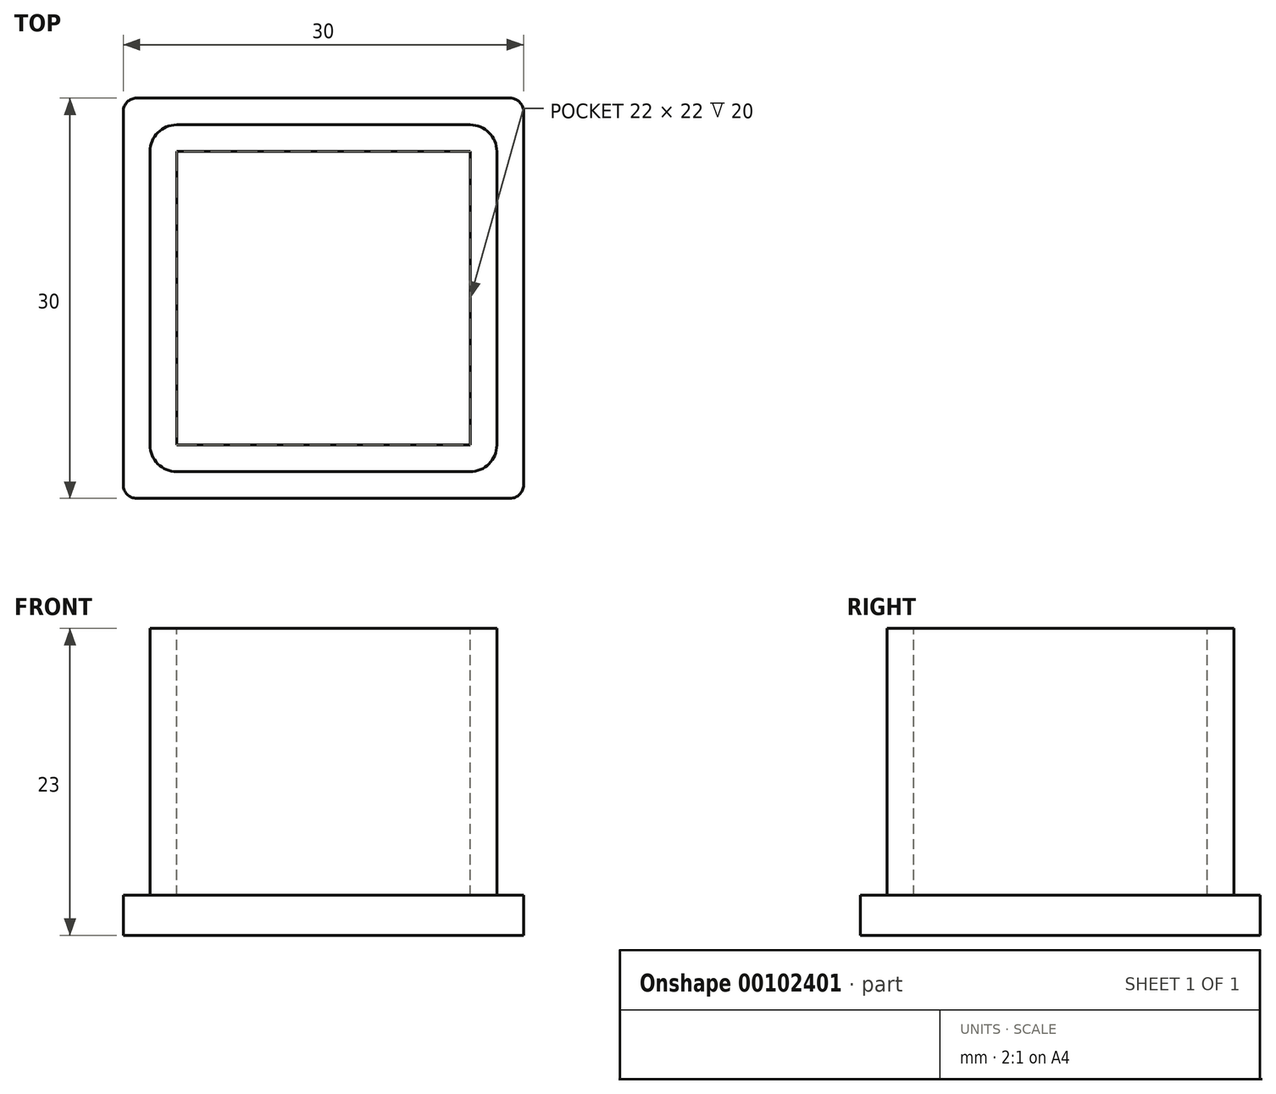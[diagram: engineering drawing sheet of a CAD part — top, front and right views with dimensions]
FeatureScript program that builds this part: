
annotation { "Feature Type Name" : "Feature", "Feature Type Description" : "" }
export const myFeature = defineFeature(function(context is Context, id is Id, definition is map)
    precondition{}
    {
        {
            var Q0;
            Q0=qCreatedBy(makeId("Top.planeOp"),FACE);
            var sketch = newSketch(context, id + "F0", { "sketchPlane" : qUnion([Q0])});
            skLineSegment(sketch, "E0.bottom", {"start": v(15, 15) * mm, "end": v(-15, 15) * mm});
            skLineSegment(sketch, "E0.top", {"start": v(15, -15) * mm, "end": v(-15, -15) * mm});
            skLineSegment(sketch, "E0.left", {"start": v(15, 15) * mm, "end": v(15, -15) * mm});
            skLineSegment(sketch, "E0.right", {"start": v(-15, 15) * mm, "end": v(-15, -15) * mm});
            skPoint(sketch, "E0.middle", {"position": v(0, 0) * mm});
            skSolve(sketch);
        }
        {
            var Q0;
            Q0=makeQuery(id+"F0.imprint","IMPRINT",FACE,{"disambiguationData":[TD([[makeQuery(id+"F0.imprint","IMPRINT",EDGE,{"derivedFrom":sQuery(id+"F0.wireOp",EDGE,"E0.bottom")}),1.0]])]});
            extrude(context, id + "F1", {"entities" : qUnion([Q0]), "depth" : 3 * mm});
        }
        {
            var Q0;
            Q0=makeQuery(id+"F1.opExtrude","SWEPT_EDGE",EDGE,{"disambiguationData":[OSD([sQuery(id+"F0.wireOp",EDGE,"E0.bottom"),sQuery(id+"F0.wireOp",EDGE,"E0.right")])]});
            var Q1;
            Q1=makeQuery(id+"F1.opExtrude","SWEPT_EDGE",EDGE,{"disambiguationData":[OSD([sQuery(id+"F0.wireOp",EDGE,"E0.top"),sQuery(id+"F0.wireOp",EDGE,"E0.right")])]});
            var Q2;
            Q2=makeQuery(id+"F1.opExtrude","SWEPT_EDGE",EDGE,{"disambiguationData":[OSD([sQuery(id+"F0.wireOp",EDGE,"E0.top"),sQuery(id+"F0.wireOp",EDGE,"E0.left")])]});
            var Q3;
            Q3=makeQuery(id+"F1.opExtrude","SWEPT_EDGE",EDGE,{"disambiguationData":[OSD([sQuery(id+"F0.wireOp",EDGE,"E0.bottom"),sQuery(id+"F0.wireOp",EDGE,"E0.left")])]});
            fillet(context, id + "F2", {"entities" : qUnion([Q0, Q1, Q2, Q3]), "radius" : 1 * mm, "tangentPropagation" : true, "allowEdgeOverflow" : false});
        }
        {
            var Q0;
            Q0=makeQuery(id+"F1.opExtrude","CAP_FACE",FACE,{"disambiguationData":[OSD([sQuery(id+"F0.wireOp",EDGE,"E0.bottom"),sQuery(id+"F0.wireOp",EDGE,"E0.top"),sQuery(id+"F0.wireOp",EDGE,"E0.left"),sQuery(id+"F0.wireOp",EDGE,"E0.right")])],"isStart":false});
            var sketch = newSketch(context, id + "F3", { "sketchPlane" : qUnion([Q0])});
            skLineSegment(sketch, "E1.0", {"start": v(13, -13) * mm, "end": v(13, 13) * mm});
            skLineSegment(sketch, "E1.1", {"start": v(-13, -13) * mm, "end": v(13, -13) * mm});
            skLineSegment(sketch, "E1.2", {"start": v(-13, 13) * mm, "end": v(-13, -13) * mm});
            skLineSegment(sketch, "E1.3", {"start": v(13, 13) * mm, "end": v(-13, 13) * mm});
            skSolve(sketch);
        }
        {
            var Q0;
            Q0 = qSketchRegion(id + "F3", true);
            var Q1;
            Q1=makeQuery(id+"F3.imprint","IMPRINT",FACE,{"disambiguationData":[TD([[makeQuery(id+"F3.imprint","IMPRINT",EDGE,{"derivedFrom":sQuery(id+"F3.wireOp",EDGE,"E1.0")}),1.0]])]});
            extrude(context, id + "F4", {"entities" : qUnion([Q0, Q1]), "operationType" : NewBodyOperationType.ADD, "depth" : 20 * mm});
        }
        {
            var Q0;
            Q0=makeQuery(id+"F4.opExtrude","SWEPT_EDGE",EDGE,{"disambiguationData":[OSD([sQuery(id+"F3.wireOp",EDGE,"E1.1"),sQuery(id+"F3.wireOp",EDGE,"E1.2")])]});
            var Q1;
            Q1=makeQuery(id+"F4.opExtrude","SWEPT_EDGE",EDGE,{"disambiguationData":[OSD([sQuery(id+"F3.wireOp",EDGE,"E1.0"),sQuery(id+"F3.wireOp",EDGE,"E1.1")])]});
            var Q2;
            Q2=makeQuery(id+"F4.opExtrude","SWEPT_EDGE",EDGE,{"disambiguationData":[OSD([sQuery(id+"F3.wireOp",EDGE,"E1.0"),sQuery(id+"F3.wireOp",EDGE,"E1.3")])]});
            var Q3;
            Q3=makeQuery(id+"F4.opExtrude","SWEPT_EDGE",EDGE,{"disambiguationData":[OSD([sQuery(id+"F3.wireOp",EDGE,"E1.2"),sQuery(id+"F3.wireOp",EDGE,"E1.3")])]});
            fillet(context, id + "F5", {"entities" : qUnion([Q0, Q1, Q2, Q3]), "radius" : 2 * mm, "tangentPropagation" : true, "allowEdgeOverflow" : false});
        }
        {
            var Q0;
            Q0=makeQuery(id+"F4.opExtrude","CAP_FACE",FACE,{"disambiguationData":[OSD([sQuery(id+"F3.wireOp",EDGE,"E1.0"),sQuery(id+"F3.wireOp",EDGE,"E1.1"),sQuery(id+"F3.wireOp",EDGE,"E1.2"),sQuery(id+"F3.wireOp",EDGE,"E1.3")])],"isStart":false});
            var sketch = newSketch(context, id + "F6", { "sketchPlane" : qUnion([Q0])});
            skLineSegment(sketch, "E2.0", {"start": v(-11, -11) * mm, "end": v(11, -11) * mm});
            skLineSegment(sketch, "E2.1", {"start": v(-11, 11) * mm, "end": v(-11, -11) * mm});
            skLineSegment(sketch, "E2.2", {"start": v(11, 11) * mm, "end": v(-11, 11) * mm});
            skLineSegment(sketch, "E2.3", {"start": v(11, -11) * mm, "end": v(11, 11) * mm});
            skSolve(sketch);
        }
        {
            var Q0;
            Q0=makeQuery(id+"F6.imprint","IMPRINT",FACE,{"disambiguationData":[TD([[makeQuery(id+"F6.imprint","IMPRINT",EDGE,{"derivedFrom":sQuery(id+"F6.wireOp",EDGE,"E2.0")}),1.0]])]});
            var Q1;
            Q1=makeQuery(id+"F1.opExtrude","CAP_FACE",FACE,{"disambiguationData":[OSD([sQuery(id+"F0.wireOp",EDGE,"E0.bottom"),sQuery(id+"F0.wireOp",EDGE,"E0.top"),sQuery(id+"F0.wireOp",EDGE,"E0.left"),sQuery(id+"F0.wireOp",EDGE,"E0.right")])],"isStart":false});
            extrude(context, id + "F7", {"entities" : qUnion([Q0]), "operationType" : NewBodyOperationType.REMOVE, "endBound" : BoundingType.UP_TO_SURFACE, "oppositeDirection" : true, "endBoundEntityFace" : qUnion([Q1]), "depth" : 25 * mm});
        }
    });
